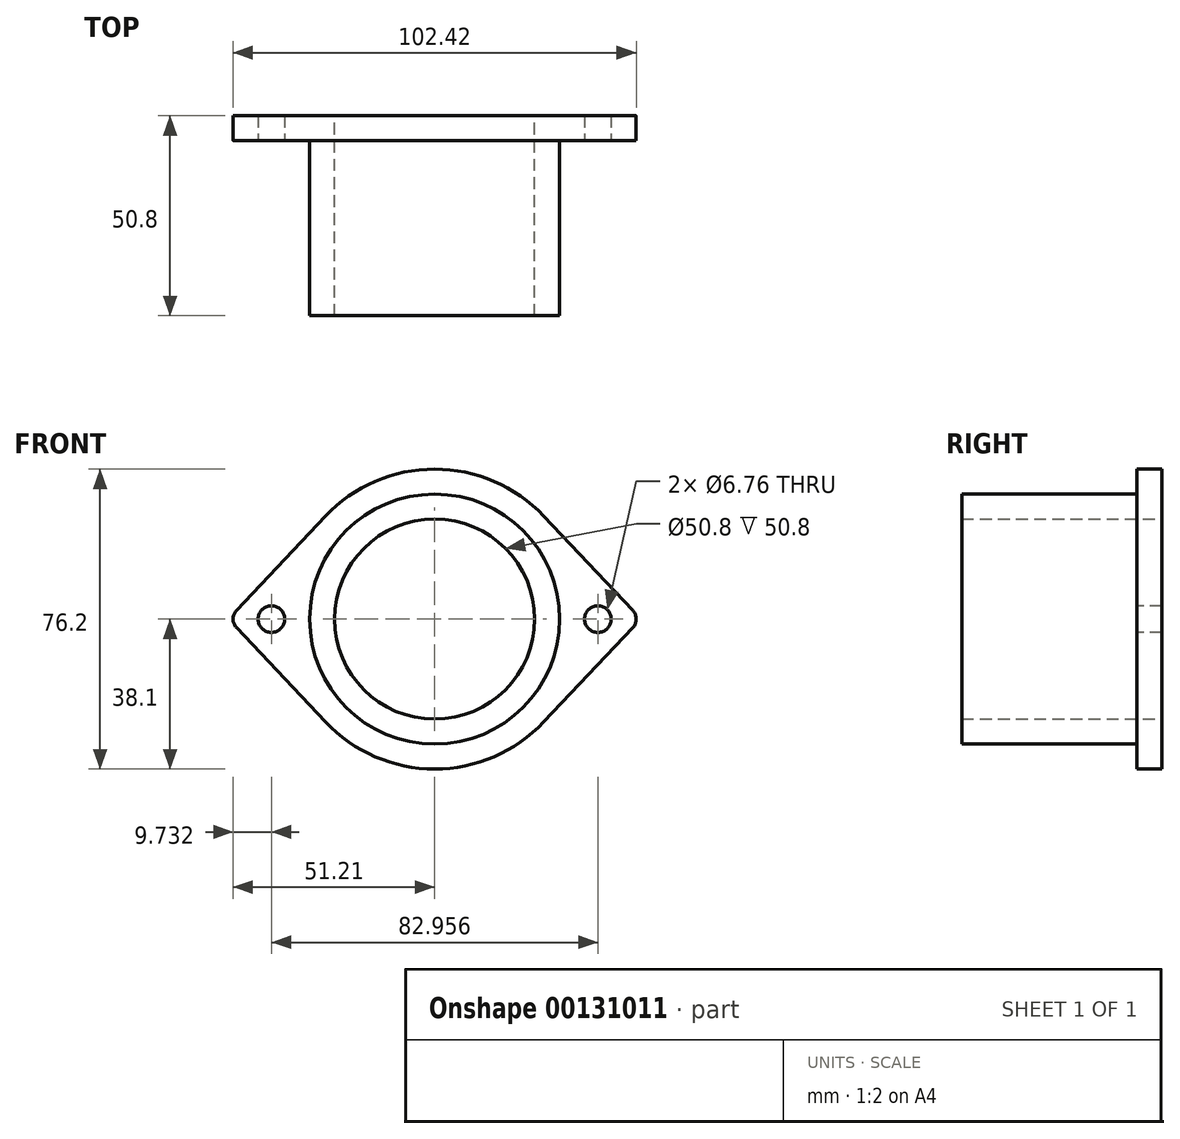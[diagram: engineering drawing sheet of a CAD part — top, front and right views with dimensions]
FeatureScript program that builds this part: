
annotation { "Feature Type Name" : "Feature", "Feature Type Description" : "" }
export const myFeature = defineFeature(function(context is Context, id is Id, definition is map)
    precondition{}
    {
        {
            var Q0;
            Q0=qCreatedBy(makeId("Front.planeOp"),FACE);
            var sketch = newSketch(context, id + "F0", { "sketchPlane" : qUnion([Q0])});
            skCircle(sketch, "E0", {"center": v(0, 0) * mm, "radius": 38.1 * mm});
            skLineSegment(sketch, "E1", {"start": v(-44.86, 0) * mm, "end": v(-48.03, 0) * mm});
            skLineSegment(sketch, "E2", {"start": v(44.86, 0) * mm, "end": v(48.03, 0) * mm});
            skCircle(sketch, "E3", {"center": v(-48.03, 0) * mm, "radius": 3.18 * mm});
            skCircle(sketch, "E4", {"center": v(48.03, 0) * mm, "radius": 3.18 * mm});
            skLineSegment(sketch, "E5", {"start": v(-50.34, -2.18) * mm, "end": v(-27.7, -26.16) * mm});
            skLineSegment(sketch, "E6", {"start": v(-50.34, 2.18) * mm, "end": v(-27.7, 26.16) * mm});
            skLineSegment(sketch, "E7", {"start": v(50.34, 2.18) * mm, "end": v(27.7, 26.16) * mm});
            skLineSegment(sketch, "E8", {"start": v(50.34, -2.18) * mm, "end": v(27.7, -26.16) * mm});
            skSolve(sketch);
        }
        {
            var Q0;
            Q0 = qSketchRegion(id + "F0", true);
            extrude(context, id + "F1", {"entities" : qUnion([Q0]), "depth" : 6.35 * mm});
        }
        {
            var Q0;
            Q0=qCreatedBy(makeId("Front.planeOp"),FACE);
            var sketch = newSketch(context, id + "F2", { "sketchPlane" : qUnion([Q0])});
            skCircle(sketch, "E9", {"center": v(0, 0) * mm, "radius": 25.4 * mm});
            skCircle(sketch, "E10", {"center": v(0, 0) * mm, "radius": 31.75 * mm});
            skSolve(sketch);
        }
        {
            var Q0;
            Q0 = qSketchRegion(id + "F2", true);
            extrude(context, id + "F3", {"entities" : qUnion([Q0]), "operationType" : NewBodyOperationType.ADD, "depth" : 50.8 * mm});
        }
        {
            var Q0;
            Q0=qCreatedBy(makeId("Right.planeOp"),FACE);
            cPlane(context, id + "F4", {"entities" : qUnion([Q0]), "cplaneType" : CPlaneType.OFFSET, "offset" : 127 * mm, "width" : 152.4 * mm, "height" : 152.4 * mm});
        }
        {
            var Q0;
            Q0=makeQuery(id+"F3.boolean.opBoolean","SPLIT",FACE,{"disambiguationData":[TD([makeQuery(id+"F3.opExtrude","SWEPT_FACE",FACE,{"disambiguationData":[OSD([sQuery(id+"F2.wireOp",EDGE,"E9")])]})])],"derivedFrom":makeQuery(id+"F1.opExtrude","CAP_FACE",FACE,{"disambiguationData":[OSD([sQuery(id+"F0.wireOp",EDGE,"E0"),sQuery(id+"F0.wireOp",EDGE,"E3"),sQuery(id+"F0.wireOp",EDGE,"E4"),sQuery(id+"F0.wireOp",EDGE,"E5"),sQuery(id+"F0.wireOp",EDGE,"E6"),sQuery(id+"F0.wireOp",EDGE,"E7"),sQuery(id+"F0.wireOp",EDGE,"E8")])],"isStart":false})});
            extrude(context, id + "F5", {"entities" : qUnion([Q0]), "operationType" : NewBodyOperationType.REMOVE, "oppositeDirection" : true, "depth" : 127 * mm});
        }
        {
            var Q0;
            Q0=qCreatedBy(makeId("Front.planeOp"),FACE);
            cPlane(context, id + "F6", {"entities" : qUnion([Q0]), "cplaneType" : CPlaneType.OFFSET, "offset" : 127 * mm, "width" : 152.4 * mm, "height" : 152.4 * mm});
        }
        {
            var Q0;
            Q0=qCreatedBy(id+"F6.planeOp",FACE);
            var sketch = newSketch(context, id + "F7", { "sketchPlane" : qUnion([Q0])});
            skCircle(sketch, "E11", {"center": v(-41.48, 0) * mm, "radius": 3.38 * mm});
            skCircle(sketch, "E12", {"center": v(41.48, 0) * mm, "radius": 3.38 * mm});
            skSolve(sketch);
        }
        {
            var Q0;
            Q0=makeQuery(id+"F7.imprint","IMPRINT",FACE,{"disambiguationData":[TD([[makeQuery(id+"F7.imprint","IMPRINT",EDGE,{"derivedFrom":sQuery(id+"F7.wireOp",EDGE,"E11")}),1.0]])]});
            var Q1;
            Q1=makeQuery(id+"F7.imprint","IMPRINT",FACE,{"disambiguationData":[TD([[makeQuery(id+"F7.imprint","IMPRINT",EDGE,{"derivedFrom":sQuery(id+"F7.wireOp",EDGE,"E12")}),1.0]])]});
            extrude(context, id + "F8", {"entities" : qUnion([Q0, Q1]), "operationType" : NewBodyOperationType.REMOVE, "oppositeDirection" : true, "depth" : 127 * mm});
        }
    });
